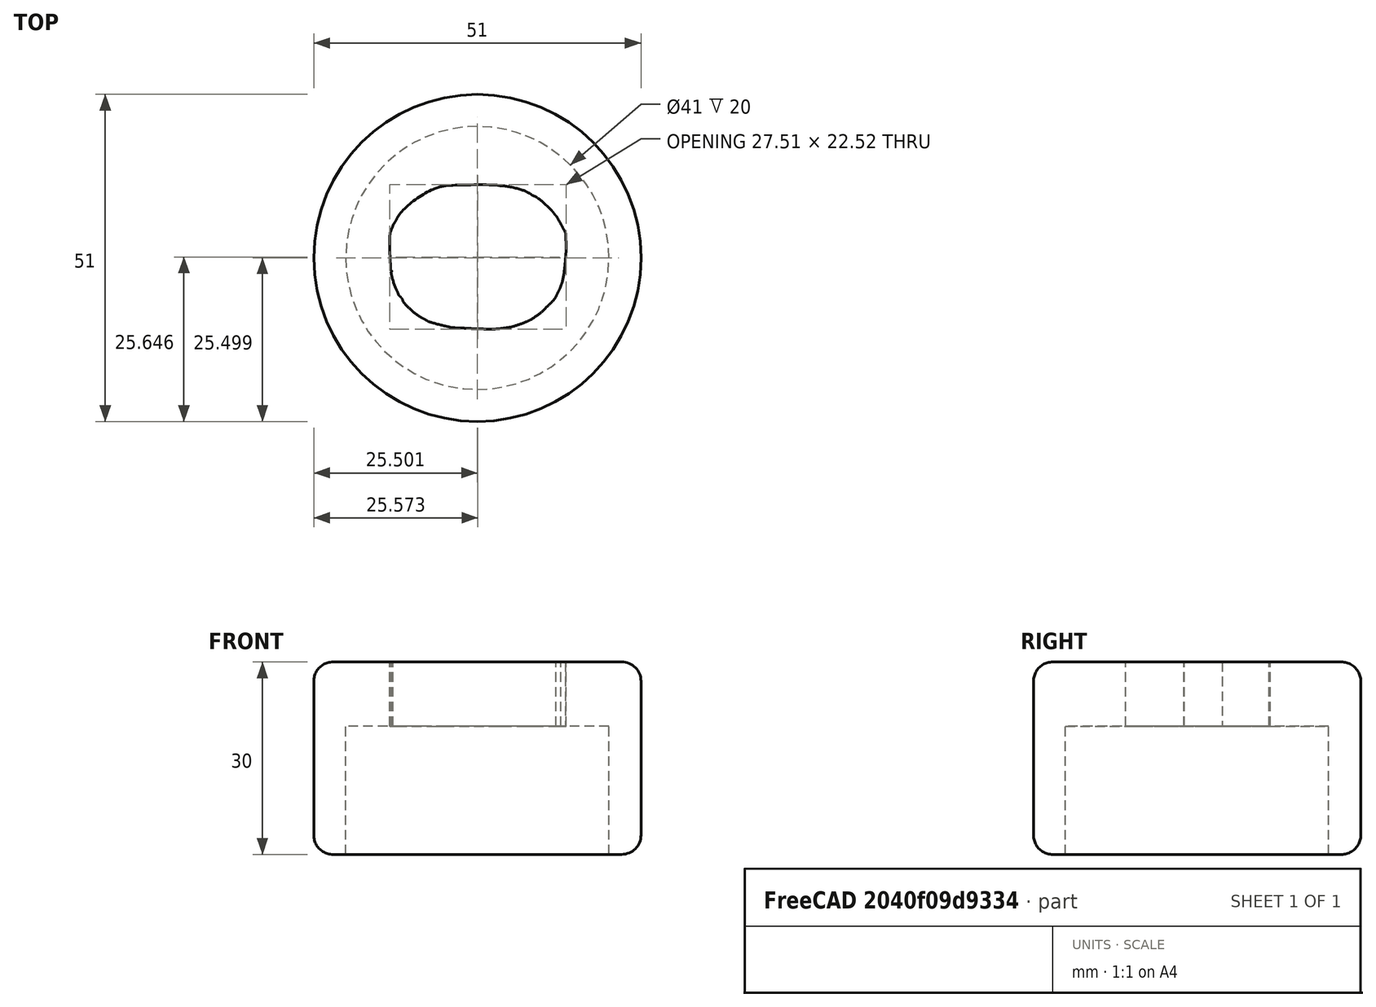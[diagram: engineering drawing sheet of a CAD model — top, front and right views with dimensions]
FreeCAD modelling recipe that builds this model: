
FCSTD DOCUMENT  (FreeCAD 0.16R6706 (Git))
Label: Capat power bank 02
License: All rights reserved
LicenseURL: http://en.wikipedia.org/wiki/All_rights_reserved
objects: Part::Cylinder×2, Part::Cut×2, Part::Feature×1, Part::FeaturePython×1, Part::Extrusion×1, Part::Fillet×1
note: 8 computed .brp shape members not serialized (recipe doc carries the construction recipe); baked Part::Feature solids carry a one-line shape summary decoded from their .brp

FEATURE [Part::Cylinder] Cylinder  label="Cilindru"
  Angle = 360
  Height = 30
  Radius = 25.5
FEATURE [Part::Cylinder] Cylinder001  label="Cilindru001"
  Angle = 360
  Height = 20
  Radius = 20.5
FEATURE [Part::Cut] Cut
  Base = -> Cylinder
  Placement = pos=(-57.9393,61.1591,60) rot=(0,0,1;0rad)
  Tool = -> Cylinder001
FEATURE [Part::Feature] Face001
  shape: bbox 91.84 x 75.58 x 2e-07 mm, 1 faces, 0 solids (baked)
FEATURE [Part::FeaturePython] Clone001  label="Clone of Face001"  # Draft clone (typed FeaturePython)
  Objects = -> [Face001]
  Placement = pos=(-91.8,78.5671,90) rot=(0,0,1;0rad)
  Scale = (0.3,0.3,1)
FEATURE [Part::Extrusion] Extrude
  Base = -> Clone001
  Dir = (0,0,-10)
  Solid = false
FEATURE [Part::Cut] Cut001
  Base = -> Cut
  Tool = -> Extrude
FEATURE [Part::Fillet] Fillet
  Base = -> Cut001
  Edges = 2 edges r=3: [Edge1,Edge3]
